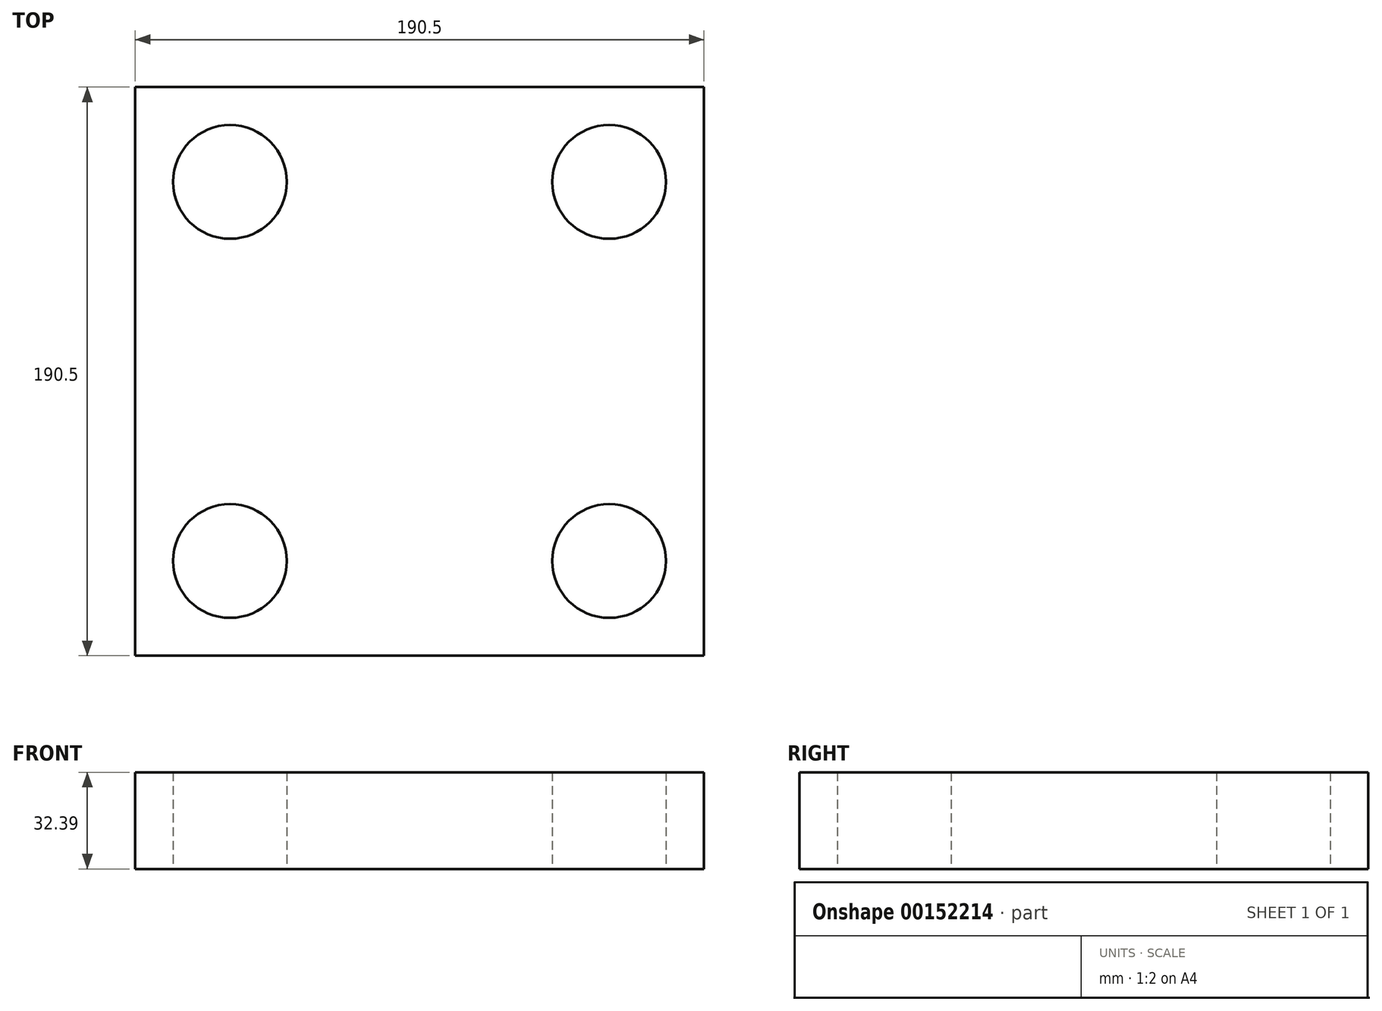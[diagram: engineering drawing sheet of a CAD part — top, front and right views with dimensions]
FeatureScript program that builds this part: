
annotation { "Feature Type Name" : "Feature", "Feature Type Description" : "" }
export const myFeature = defineFeature(function(context is Context, id is Id, definition is map)
    precondition{}
    {
        {
            var Q0;
            Q0=qCreatedBy(makeId("Top.planeOp"),FACE);
            var sketch = newSketch(context, id + "F0", { "sketchPlane" : qUnion([Q0])});
            skCircle(sketch, "E0", {"center": v(63.5, 63.5) * mm, "radius": 19.05 * mm});
            skCircle(sketch, "E1", {"center": v(63.5, -63.5) * mm, "radius": 19.05 * mm});
            skCircle(sketch, "E2", {"center": v(-63.5, -63.5) * mm, "radius": 19.05 * mm});
            skCircle(sketch, "E3", {"center": v(-63.5, 63.5) * mm, "radius": 19.05 * mm});
            skLineSegment(sketch, "E4", {"start": v(-63.5, 63.5) * mm, "end": v(-63.5, -63.5) * mm, "construction": true});
            skLineSegment(sketch, "E5", {"start": v(-63.5, -63.5) * mm, "end": v(63.5, -63.5) * mm, "construction": true});
            skLineSegment(sketch, "E6", {"start": v(63.5, -63.5) * mm, "end": v(63.5, 63.5) * mm, "construction": true});
            skLineSegment(sketch, "E7", {"start": v(63.5, 63.5) * mm, "end": v(-63.5, 63.5) * mm, "construction": true});
            skLineSegment(sketch, "E8", {"start": v(0, 63.5) * mm, "end": v(0, 0) * mm, "construction": true});
            skLineSegment(sketch, "E9", {"start": v(0, 0) * mm, "end": v(-63.5, 0) * mm});
            skLineSegment(sketch, "E10", {"start": v(63.5, 0) * mm, "end": v(0, 0) * mm});
            skLineSegment(sketch, "E11.bottom", {"start": v(95.25, 95.25) * mm, "end": v(-95.25, 95.25) * mm});
            skLineSegment(sketch, "E11.top", {"start": v(95.25, -95.25) * mm, "end": v(-95.25, -95.25) * mm});
            skLineSegment(sketch, "E11.left", {"start": v(95.25, 95.25) * mm, "end": v(95.25, -95.25) * mm});
            skLineSegment(sketch, "E11.right", {"start": v(-95.25, 95.25) * mm, "end": v(-95.25, -95.25) * mm});
            skPoint(sketch, "E11.middle", {"position": v(0, 0) * mm});
            skSolve(sketch);
        }
        {
            var Q0;
            Q0 = qSketchRegion(id + "F0", true);
            extrude(context, id + "F1", {"entities" : qUnion([Q0]), "depth" : 32.38 * mm});
        }
    });
